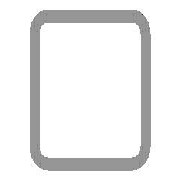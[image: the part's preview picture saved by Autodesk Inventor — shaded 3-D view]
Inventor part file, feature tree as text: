
AUTODESK INVENTOR PART (.ipt)
format: ipt  version: 2025 (Build 290162010, 162A)  size: 131,584 bytes
history: native  units: mm (DEFAULTED — no unit token found)
features: other x4, sketch x1, plane x1
ambient origin geometry x8: Origin, YZ Plane, XZ Plane, XY Plane, X Axis, Y Axis, Z Axis, Center Point
bodies: Solid1 (feature_tree), Body (feature_tree)
feature tree (6):
  parser-record x1  (decoder bookkeeping rows leaked as tree rows — omitted from the tree; the rows remain in map.json)
  other  "Driven Length"
  other  "Start Plane"
  other  "End Plane"
  sketch  "Sketch3"  dims[d3=90.0mm d4=0.0mm d7=4.0mm d9=40.0mm d11=40.0mm d12=2.0mm d13=50.0mm d14=140.0mm d15=20.0mm d16=20.0mm d17=90.0deg d18=90.0mm]
  plane  "Work Plane3"
